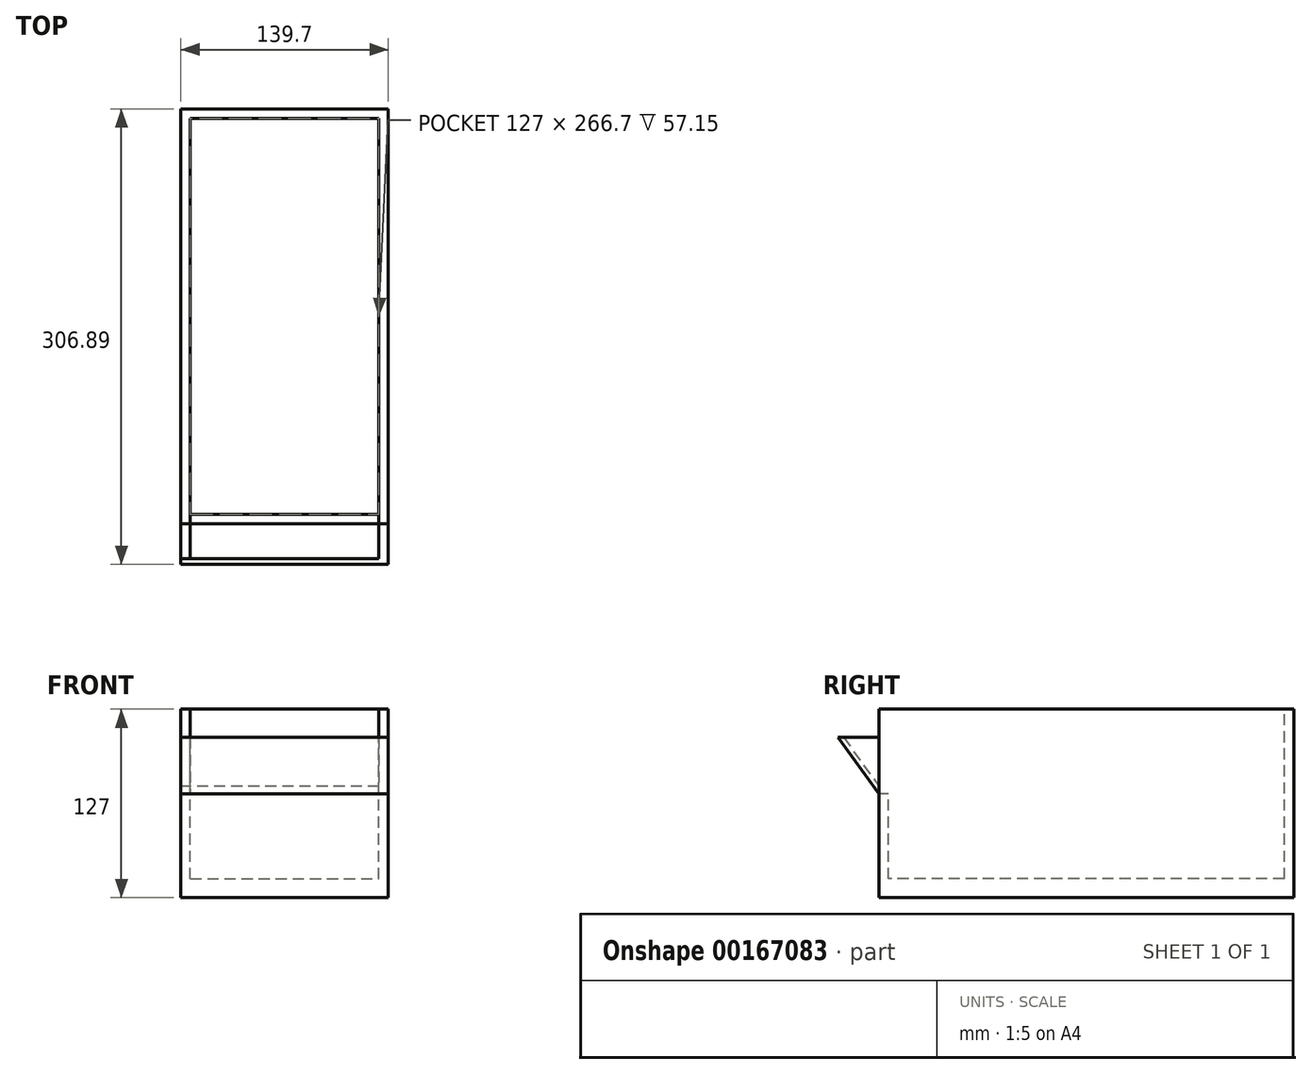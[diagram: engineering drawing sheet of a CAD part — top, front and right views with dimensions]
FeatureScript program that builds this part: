
annotation { "Feature Type Name" : "Feature", "Feature Type Description" : "" }
export const myFeature = defineFeature(function(context is Context, id is Id, definition is map)
    precondition{}
    {
        {
            var Q0;
            Q0=qCreatedBy(makeId("Top.planeOp"),FACE);
            var sketch = newSketch(context, id + "F0", { "sketchPlane" : qUnion([Q0])});
            skLineSegment(sketch, "E0.bottom", {"start": v(69.85, 139.7) * mm, "end": v(-69.85, 139.7) * mm});
            skLineSegment(sketch, "E0.top", {"start": v(69.85, -139.7) * mm, "end": v(-69.85, -139.7) * mm});
            skLineSegment(sketch, "E0.left", {"start": v(69.85, 139.7) * mm, "end": v(69.85, -139.7) * mm});
            skLineSegment(sketch, "E0.right", {"start": v(-69.85, 139.7) * mm, "end": v(-69.85, -139.7) * mm});
            skPoint(sketch, "E0.middle", {"position": v(0, 0) * mm});
            skSolve(sketch);
        }
        {
            var Q0;
            Q0 = qSketchRegion(id + "F0", true);
            extrude(context, id + "F1", {"entities" : qUnion([Q0]), "depth" : 127 * mm});
        }
        {
            var Q0;
            Q0=makeQuery(id+"F1.opExtrude","CAP_FACE",FACE,{"disambiguationData":[OSD([sQuery(id+"F0.wireOp",EDGE,"E0.bottom"),sQuery(id+"F0.wireOp",EDGE,"E0.top"),sQuery(id+"F0.wireOp",EDGE,"E0.left"),sQuery(id+"F0.wireOp",EDGE,"E0.right")])],"isStart":false});
            var sketch = newSketch(context, id + "F2", { "sketchPlane" : qUnion([Q0])});
            skLineSegment(sketch, "E1", {"start": v(-69.85, 139.7) * mm, "end": v(-63.5, 139.7) * mm});
            skLineSegment(sketch, "E2", {"start": v(-63.5, 139.7) * mm, "end": v(-63.5, 133.35) * mm});
            skLineSegment(sketch, "E3.bottom", {"start": v(-63.5, 133.35) * mm, "end": v(63.5, 133.35) * mm});
            skLineSegment(sketch, "E3.top", {"start": v(-63.5, -133.35) * mm, "end": v(63.5, -133.35) * mm});
            skLineSegment(sketch, "E3.left", {"start": v(-63.5, 133.35) * mm, "end": v(-63.5, -133.35) * mm});
            skLineSegment(sketch, "E3.right", {"start": v(63.5, 133.35) * mm, "end": v(63.5, -133.35) * mm});
            skSolve(sketch);
        }
        {
            var Q0;
            Q0 = qSketchRegion(id + "F2", true);
            extrude(context, id + "F3", {"entities" : qUnion([Q0]), "operationType" : NewBodyOperationType.REMOVE, "oppositeDirection" : true, "depth" : 114.3 * mm});
        }
        {
            var Q0;
            Q0=makeQuery(id+"F1.opExtrude","SWEPT_FACE",FACE,{"disambiguationData":[OSD([sQuery(id+"F0.wireOp",EDGE,"E0.top")])]});
            var sketch = newSketch(context, id + "F4", { "sketchPlane" : qUnion([Q0])});
            skLineSegment(sketch, "E4", {"start": v(-69.85, 127) * mm, "end": v(-63.5, 127) * mm});
            skLineSegment(sketch, "E5", {"start": v(-63.5, 127) * mm, "end": v(-63.5, 69.85) * mm});
            skLineSegment(sketch, "E6", {"start": v(-63.5, 69.85) * mm, "end": v(63.5, 69.85) * mm});
            skLineSegment(sketch, "E7", {"start": v(63.5, 69.85) * mm, "end": v(63.5, 127) * mm});
            skLineSegment(sketch, "E8", {"start": v(63.5, 127) * mm, "end": v(-63.5, 127) * mm});
            skSolve(sketch);
        }
        {
            var Q0;
            Q0=makeQuery(id+"F4.imprint","IMPRINT",FACE,{"disambiguationData":[TD([[makeQuery(id+"F4.imprint","IMPRINT",EDGE,{"derivedFrom":sQuery(id+"F4.wireOp",EDGE,"E5")}),1.0]])]});
            extrude(context, id + "F5", {"entities" : qUnion([Q0]), "operationType" : NewBodyOperationType.REMOVE, "oppositeDirection" : true, "depth" : 25.4 * mm});
        }
        {
            var Q0;
            Q0=makeQuery(id+"F1.opExtrude","SWEPT_FACE",FACE,{"disambiguationData":[OSD([sQuery(id+"F0.wireOp",EDGE,"E0.left")])]});
            var sketch = newSketch(context, id + "F6", { "sketchPlane" : qUnion([Q0])});
            skLineSegment(sketch, "E9", {"start": v(-139.7, 127) * mm, "end": v(-139.7, 69.85) * mm});
            skLineSegment(sketch, "E10", {"start": v(-139.7, 69.85) * mm, "end": v(-180.93, 127) * mm});
            skLineSegment(sketch, "E11", {"start": v(-139.7, 127) * mm, "end": v(-139.7, 107.95) * mm});
            skLineSegment(sketch, "E12", {"start": v(-139.7, 107.95) * mm, "end": v(-167.19, 107.95) * mm});
            skSolve(sketch);
        }
        {
            var Q0;
            {var subQ0=sQuery(id+"F6.wireOp",EDGE,"E9");Q0=makeQuery(id+"F6.imprint","IMPRINT",FACE,{"disambiguationData":[TD([[makeQuery(id+"F6.imprint","IMPRINT",EDGE,{"derivedFrom":subQ0}),-1.0]])]});}
            extrude(context, id + "F7", {"entities" : qUnion([Q0]), "oppositeDirection" : true, "depth" : 139.7 * mm});
        }
        {
            var Q0;
            Q0=makeQuery(id+"F7.opExtrude","CAP_FACE",FACE,{"disambiguationData":[OSD([sQuery(id+"F6.wireOp",EDGE,"E9"),sQuery(id+"F6.wireOp",EDGE,"E10"),sQuery(id+"F6.wireOp",EDGE,"E12")])],"isStart":false});
            var sketch = newSketch(context, id + "F8", { "sketchPlane" : qUnion([Q0])});
            skLineSegment(sketch, "E13", {"start": v(139.7, 108.74) * mm, "end": v(139.7, 107.95) * mm});
            skLineSegment(sketch, "E14", {"start": v(139.7, 108.74) * mm, "end": v(167.75, 108.74) * mm});
            skLineSegment(sketch, "E15", {"start": v(167.75, 108.74) * mm, "end": v(163.94, 108.74) * mm});
            skLineSegment(sketch, "E16", {"start": v(163.94, 108.74) * mm, "end": v(139.7, 75.13) * mm});
            skSolve(sketch);
        }
        {
            var Q0;
            {var subQ0=sQuery(id+"F8.wireOp",EDGE,"E16");Q0=makeQuery(id+"F8.imprint","IMPRINT",FACE,{"disambiguationData":[TD([[makeQuery(id+"F8.imprint","IMPRINT",EDGE,{"derivedFrom":subQ0}),-1.0]])]});}
            extrude(context, id + "F9", {"entities" : qUnion([Q0]), "operationType" : NewBodyOperationType.REMOVE, "oppositeDirection" : true, "depth" : 133.35 * mm});
        }
        {
            var Q0;
            Q0=makeQuery(id+"F7.opExtrude","CAP_FACE",FACE,{"disambiguationData":[OSD([sQuery(id+"F6.wireOp",EDGE,"E9"),sQuery(id+"F6.wireOp",EDGE,"E10"),sQuery(id+"F6.wireOp",EDGE,"E12")])],"isStart":false});
            var sketch = newSketch(context, id + "F10", { "sketchPlane" : qUnion([Q0])});
            skLineSegment(sketch, "E17", {"start": v(163.38, 107.95) * mm, "end": v(139.7, 75.13) * mm});
            skLineSegment(sketch, "E18", {"start": v(139.7, 75.13) * mm, "end": v(139.7, 107.95) * mm});
            skLineSegment(sketch, "E19", {"start": v(139.7, 107.95) * mm, "end": v(163.38, 107.95) * mm});
            skSolve(sketch);
        }
        {
            var Q0;
            Q0 = qSketchRegion(id + "F10", true);
            extrude(context, id + "F11", {"entities" : qUnion([Q0]), "oppositeDirection" : true, "depth" : 6.35 * mm});
        }
        {
            var Q0;
            Q0 = qSketchRegion(id + "F10", true);
            extrude(context, id + "F12", {"entities" : qUnion([Q0]), "oppositeDirection" : true, "depth" : 6.35 * mm});
        }
        {
            var Q0;
            Q0=makeQuery(id+"F11.opExtrude","SWEPT_BODY",BODY,{"disambiguationData":[OSD([sQuery(id+"F10.wireOp",EDGE,"E17"),sQuery(id+"F10.wireOp",EDGE,"E18"),sQuery(id+"F10.wireOp",EDGE,"E19")])]});
            deleteBodies(context, id + "F13", {"entities" : qUnion([Q0])});
        }
    });
